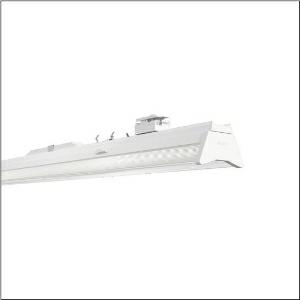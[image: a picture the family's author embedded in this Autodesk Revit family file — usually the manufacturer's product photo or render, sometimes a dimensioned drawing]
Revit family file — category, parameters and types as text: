
# Revit family: licross_r__21_performance_ho_52tm16cn4c5m_51b1
name_source: partatom
category: Lighting Fixtures
units: mm (PartAtom-declared; Revit-internal decimal feet)

## family parameters
Cut with Voids When Loaded = No
Host = Face
Light Source = No
Part Type = Normal
Room Calculation Point = No
Round Connector Dimension = Use Diameter
Shared = No

## types (1)
- --- (1 x LED, 12610 lm, 68.9 W, 4000K)
    Apparent Load = 69 VA
    CIE Flux Codes = 63 87 95 78 100
    Color Rendering = 80
    Color Temperature = 4000K
    Default Elevation = 1800 mm
    Description = Licross® 21 Performance HO, luminaire insert, of sheet steel, galvanised, coil coated, white, length: 1.500mm, width: 120mm, height: 123mm, LED rated luminous flux: 12.610lm, light colour: 840, control gear: ON/OFF Multilumen, CLOi, control gear: ECG Multilumen, with plug, 3-pole, with phase selection, mains connection: 220..240V, AC, 50/60Hz, halogen-free wiring, primary light control with lens, of plastic, primary optical cover: cover, of PMMA, light emission: direct/indirect distribution, primary light characteristic: symmetric, protection rating (complete): IP40, insulation class (complete): insulation class I (protective earthing), certification: CE, ENEC, UKCA, protection symbol: D if used in an environment without relevant dust loads with corresponding accessories, impact resistance: IK06, permissible ambient temperature for indoor applications: -35..+35°C, corresponds to IFS (International Featured Standards) requirements for safety and quality in the food industry, reducing of maximum allowable ambient temperature of 5°C with ceiling mounting, LABS conformity tested according to VDMA 24364:2018-05, packaging unit: 1 piece
    Height = 114 mm
    Lamp = 1 x LED
    Lamp Light Flux = 12610 lm
    Lamp Power = 68.9 W
    Lamp count = 1
    Length = 1500 mm
    Luminous efficacy = 183 lm/W
    Manufacturer = Siteco
    ModVariant = No
    Model = 52TM16CN4C5M
    Mounting Place = Ceiling
    Mounting Type = Pendant
    Number of Poles = 1
    OnlyDefault = Yes
    Power Factor = 1
    Product Name = Licross® 21 Performance HO
    Product group = luminaire insert
    ProductGroupID = 902
    Protection Class = Protection class I
    Protection Degree = IP 40
    RLX_Detail_Level = 1
    RlxData = <blob elided: 31793 chars, md5=17c72a4a>
    Socket = socket
    Standby Power = 0 W
    System Light Flux = 12610 lm
    System Power = 69 W
    Type Comments = factory setting: luminous flux: 100 % | (A | C | E) | 162 mA
    Type Image = l_1256138.jpg
    URL = http://relux.com
    VarID = @adj_020049
    Voltage = 0 V
    Weight = 0.00 kg
    Width = 120 mm

## geometry (parser evidence)
native form markers: Blend x4, Sweep x12
no freeform markers — native parametric forms only
